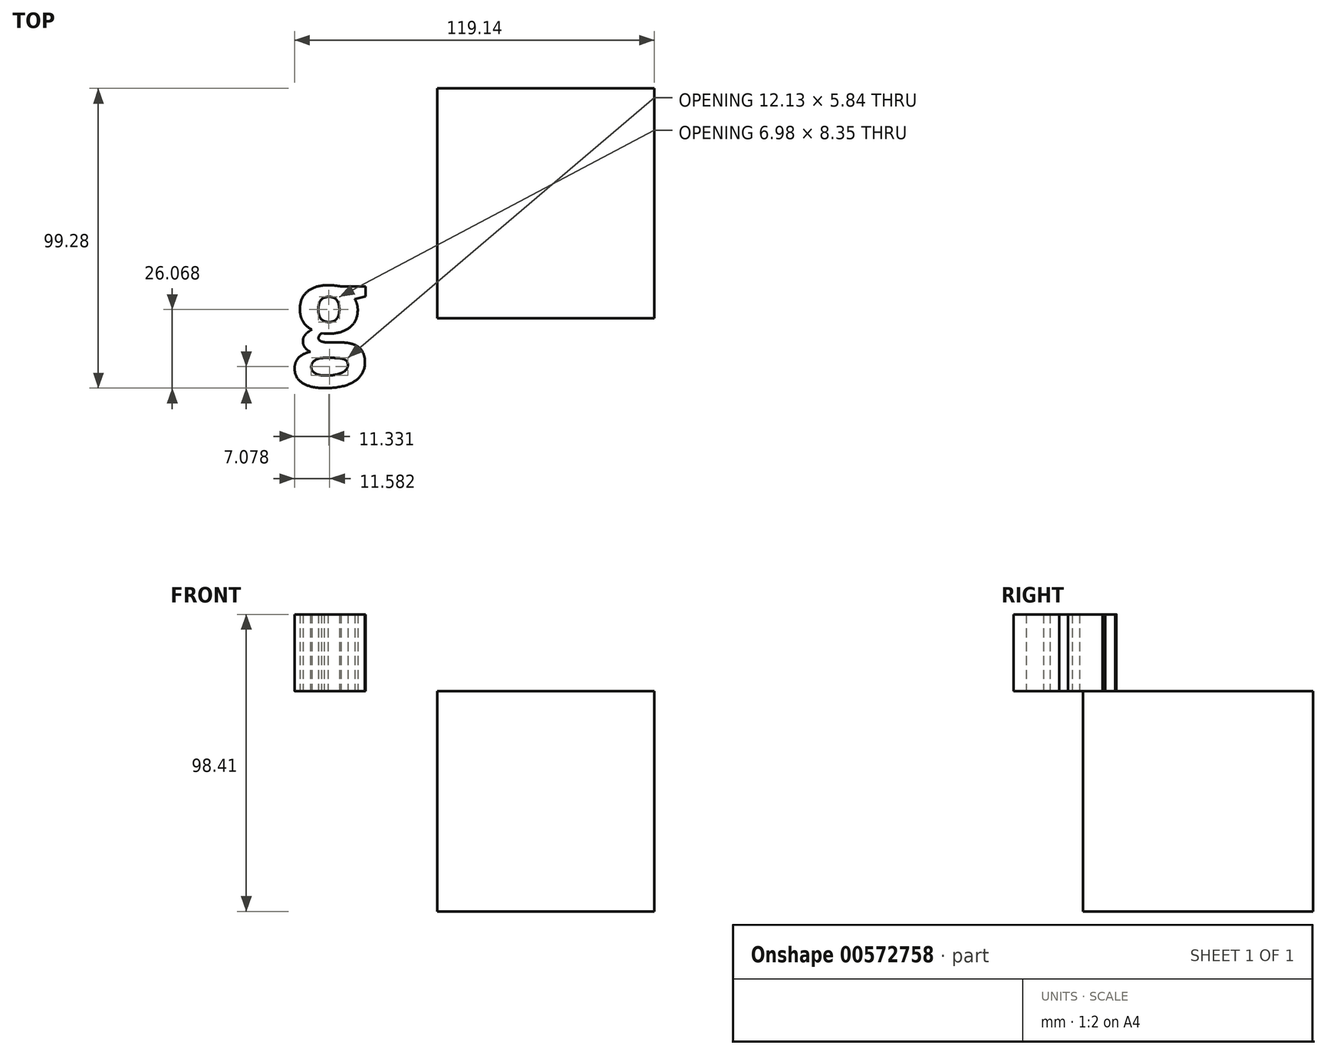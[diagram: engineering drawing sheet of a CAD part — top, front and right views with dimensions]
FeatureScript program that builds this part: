
annotation { "Feature Type Name" : "Feature", "Feature Type Description" : "" }
export const myFeature = defineFeature(function(context is Context, id is Id, definition is map)
    precondition{}
    {
        {
            var Q0;
            Q0=qCreatedBy(makeId("Front.planeOp"),FACE);
            var sketch = newSketch(context, id + "F0", { "sketchPlane" : qUnion([Q0])});
            skLineSegment(sketch, "E0.bottom", {"start": v(0, -3.4) * mm, "end": v(-71.85, -3.4) * mm});
            skLineSegment(sketch, "E0.top", {"start": v(0, 69.61) * mm, "end": v(-71.85, 69.61) * mm});
            skLineSegment(sketch, "E0.left", {"start": v(0, -3.4) * mm, "end": v(0, 69.61) * mm});
            skLineSegment(sketch, "E0.right", {"start": v(-71.85, -3.4) * mm, "end": v(-71.85, 69.61) * mm});
            skSolve(sketch);
        }
        {
            var Q0;
            Q0=makeQuery(id+"F0.imprint","IMPRINT",FACE,{"disambiguationData":[TD([[makeQuery(id+"F0.imprint","IMPRINT",EDGE,{"derivedFrom":sQuery(id+"F0.wireOp",EDGE,"E0.bottom")}),-1.0]])]});
            extrude(context, id + "F1", {"entities" : qUnion([Q0]), "depth" : 76.2 * mm, "offsetDistance" : 25.4 * mm});
        }
        {
            var Q0;
            Q0=makeQuery(id+"F1.opExtrude","SWEPT_FACE",FACE,{"disambiguationData":[OSD([sQuery(id+"F0.wireOp",EDGE,"E0.top")])]});
            var sketch = newSketch(context, id + "F2", { "sketchPlane" : qUnion([Q0])});
            skText(sketch, "E1", { "text": "germonee", "fontName": "OpenSans-Bold.ttf"});
            const initialGuessF2  = {"E1": [-0.11927, -0.08899, 1, 0, 0.03084]};
            skSetInitialGuess(sketch, initialGuessF2);
            skSolve(sketch);
        }
        {
            var Q0;
            Q0=makeQuery(id+"F2.imprint","IMPRINT",FACE,{"disambiguationData":[TD([[makeQuery(id+"F2.imprint","IMPRINT",EDGE,{"derivedFrom":sQuery(id+"F2.wireOp",EDGE,"E1.sketch_text.stroke-0")}),-1.0]])]});
            extrude(context, id + "F3", {"entities" : qUnion([Q0]), "depth" : 25.4 * mm, "offsetDistance" : 25.4 * mm});
        }
    });
